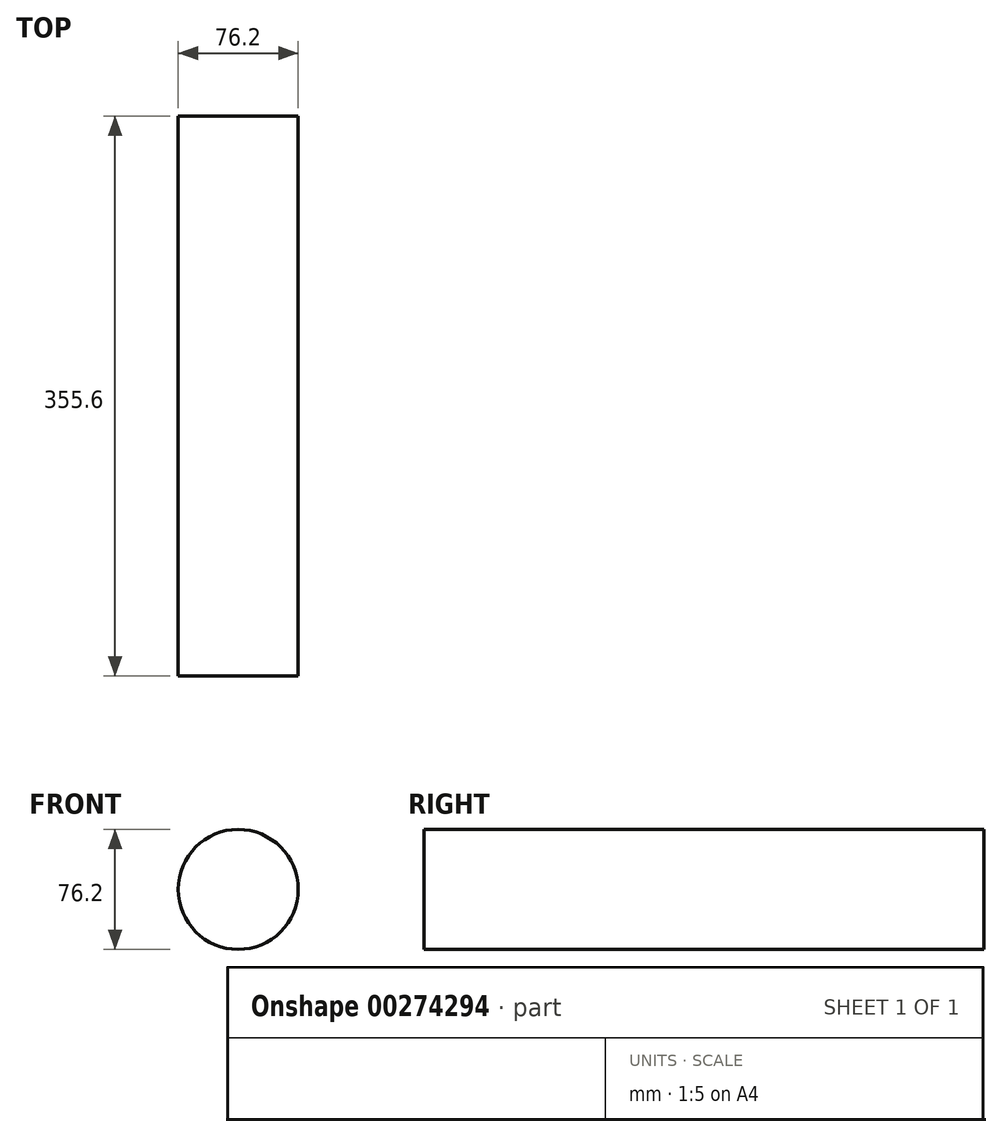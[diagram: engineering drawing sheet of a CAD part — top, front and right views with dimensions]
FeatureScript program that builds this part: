
annotation { "Feature Type Name" : "Feature", "Feature Type Description" : "" }
export const myFeature = defineFeature(function(context is Context, id is Id, definition is map)
    precondition{}
    {
        {
            var Q0;
            Q0=qCreatedBy(makeId("Front.planeOp"),FACE);
            var sketch = newSketch(context, id + "F0", { "sketchPlane" : qUnion([Q0])});
            skCircle(sketch, "E0", {"center": v(0, 0) * mm, "radius": 38.1 * mm});
            skSolve(sketch);
        }
        {
            var Q0;
            Q0 = qSketchRegion(id + "F0", true);
            extrude(context, id + "F1", {"entities" : qUnion([Q0]), "depth" : 355.6 * mm});
        }
    });
